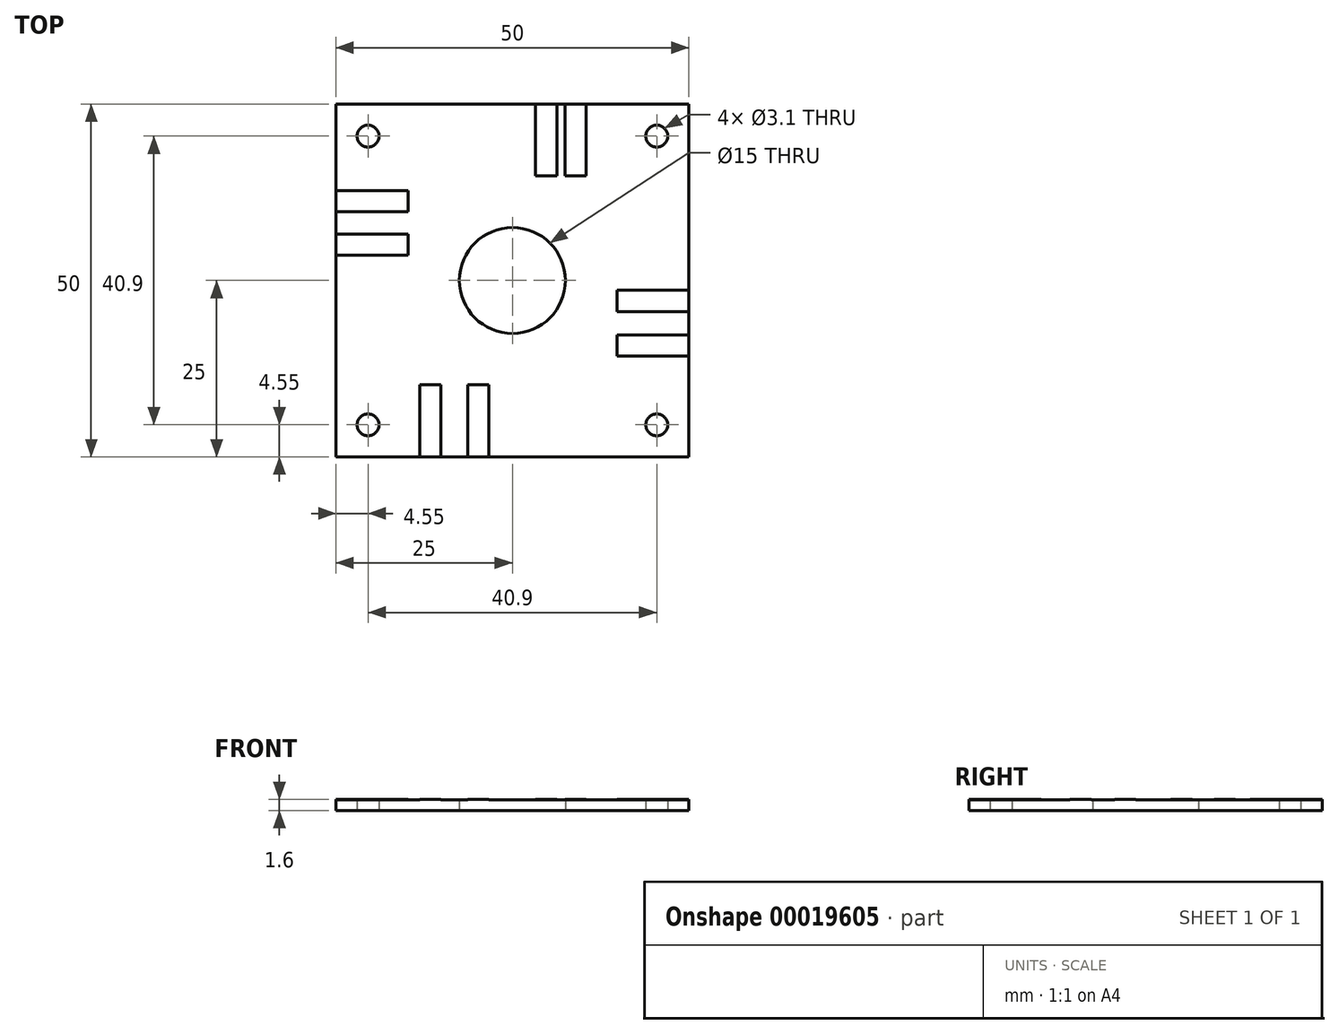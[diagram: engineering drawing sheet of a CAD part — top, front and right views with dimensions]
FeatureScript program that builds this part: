
annotation { "Feature Type Name" : "Feature", "Feature Type Description" : "" }
export const myFeature = defineFeature(function(context is Context, id is Id, definition is map)
    precondition{}
    {
        {
            var Q0;
            Q0=qCreatedBy(makeId("Top.planeOp"),FACE);
            var sketch = newSketch(context, id + "F0", { "sketchPlane" : qUnion([Q0])});
            skLineSegment(sketch, "E0.rect.bottom", {"start": v(-25, 25) * mm, "end": v(25, 25) * mm});
            skLineSegment(sketch, "E0.rect.top", {"start": v(-25, -25) * mm, "end": v(25, -25) * mm});
            skLineSegment(sketch, "E0.rect.left", {"start": v(-25, 25) * mm, "end": v(-25, -25) * mm});
            skLineSegment(sketch, "E0.rect.right", {"start": v(25, 25) * mm, "end": v(25, -25) * mm});
            skPoint(sketch, "E0.rect.middle", {"position": v(0, 0) * mm});
            skCircle(sketch, "E1", {"center": v(0, 0) * mm, "radius": 7.5 * mm});
            skCircle(sketch, "E2", {"center": v(-20.45, 20.45) * mm, "radius": 1.55 * mm});
            skCircle(sketch, "E3", {"center": v(-20.45, -20.45) * mm, "radius": 1.55 * mm});
            skCircle(sketch, "E4", {"center": v(20.45, -20.45) * mm, "radius": 1.55 * mm});
            skCircle(sketch, "E5", {"center": v(20.45, 20.45) * mm, "radius": 1.55 * mm});
            skSolve(sketch);
        }
        {
            var Q0;
            Q0=makeQuery(id+"F0.imprint","IMPRINT",FACE,{"disambiguationData":[TD([[makeQuery(id+"F0.imprint","IMPRINT",EDGE,{"derivedFrom":sQuery(id+"F0.wireOp",EDGE,"E0.rect.bottom")}),-1.0]])]});
            extrude(context, id + "F1", {"entities" : qUnion([Q0]), "depth" : 1.5 * mm});
        }
        {
            var Q0;
            Q0=makeQuery(id+"F1.opExtrude","CAP_FACE",FACE,{"disambiguationData":[OSD([sQuery(id+"F0.wireOp",EDGE,"E0.rect.bottom"),sQuery(id+"F0.wireOp",EDGE,"E0.rect.top"),sQuery(id+"F0.wireOp",EDGE,"E0.rect.left"),sQuery(id+"F0.wireOp",EDGE,"E0.rect.right"),sQuery(id+"F0.wireOp",EDGE,"E1"),sQuery(id+"F0.wireOp",EDGE,"E2"),sQuery(id+"F0.wireOp",EDGE,"E3"),sQuery(id+"F0.wireOp",EDGE,"E4"),sQuery(id+"F0.wireOp",EDGE,"E5")])],"isStart":false});
            var sketch = newSketch(context, id + "F2", { "sketchPlane" : qUnion([Q0])});
            skLineSegment(sketch, "E6.bottom", {"start": v(-13.15, -25) * mm, "end": v(-10.15, -25) * mm});
            skLineSegment(sketch, "E6.top", {"start": v(-13.15, -14.8) * mm, "end": v(-10.15, -14.8) * mm});
            skLineSegment(sketch, "E6.left", {"start": v(-13.15, -25) * mm, "end": v(-13.15, -14.8) * mm});
            skLineSegment(sketch, "E6.right", {"start": v(-10.15, -25) * mm, "end": v(-10.15, -14.8) * mm});
            skLineSegment(sketch, "E7.bottom", {"start": v(-6.35, -25) * mm, "end": v(-3.35, -25) * mm});
            skLineSegment(sketch, "E7.top", {"start": v(-6.35, -14.8) * mm, "end": v(-3.35, -14.8) * mm});
            skLineSegment(sketch, "E7.left", {"start": v(-6.35, -25) * mm, "end": v(-6.35, -14.8) * mm});
            skLineSegment(sketch, "E7.right", {"start": v(-3.35, -25) * mm, "end": v(-3.35, -14.8) * mm});
            skLineSegment(sketch, "E8.bottom", {"start": v(-25, 12.73) * mm, "end": v(-14.8, 12.73) * mm});
            skLineSegment(sketch, "E8.top", {"start": v(-25, 9.73) * mm, "end": v(-14.8, 9.73) * mm});
            skLineSegment(sketch, "E8.left", {"start": v(-25, 12.73) * mm, "end": v(-25, 9.73) * mm});
            skLineSegment(sketch, "E8.right", {"start": v(-14.8, 12.73) * mm, "end": v(-14.8, 9.73) * mm});
            skLineSegment(sketch, "E9.bottom", {"start": v(-25, 6.59) * mm, "end": v(-14.8, 6.59) * mm});
            skLineSegment(sketch, "E9.top", {"start": v(-25, 3.59) * mm, "end": v(-14.8, 3.59) * mm});
            skLineSegment(sketch, "E9.left", {"start": v(-25, 6.59) * mm, "end": v(-25, 3.59) * mm});
            skLineSegment(sketch, "E9.right", {"start": v(-14.8, 6.59) * mm, "end": v(-14.8, 3.59) * mm});
            skLineSegment(sketch, "E10.bottom", {"start": v(10.43, 25) * mm, "end": v(7.43, 25) * mm});
            skLineSegment(sketch, "E10.top", {"start": v(10.43, 14.8) * mm, "end": v(7.43, 14.8) * mm});
            skLineSegment(sketch, "E10.left", {"start": v(10.43, 25) * mm, "end": v(10.43, 14.8) * mm});
            skLineSegment(sketch, "E10.right", {"start": v(7.43, 25) * mm, "end": v(7.43, 14.8) * mm});
            skLineSegment(sketch, "E11.bottom", {"start": v(6.28, 25) * mm, "end": v(3.28, 25) * mm});
            skLineSegment(sketch, "E11.top", {"start": v(6.28, 14.8) * mm, "end": v(3.28, 14.8) * mm});
            skLineSegment(sketch, "E11.left", {"start": v(6.28, 25) * mm, "end": v(6.28, 14.8) * mm});
            skLineSegment(sketch, "E11.right", {"start": v(3.28, 25) * mm, "end": v(3.28, 14.8) * mm});
            skLineSegment(sketch, "E12.bottom", {"start": v(25, -10.7) * mm, "end": v(14.8, -10.7) * mm});
            skLineSegment(sketch, "E12.top", {"start": v(25, -7.7) * mm, "end": v(14.8, -7.7) * mm});
            skLineSegment(sketch, "E12.left", {"start": v(25, -10.7) * mm, "end": v(25, -7.7) * mm});
            skLineSegment(sketch, "E12.right", {"start": v(14.8, -10.7) * mm, "end": v(14.8, -7.7) * mm});
            skLineSegment(sketch, "E13.bottom", {"start": v(25, -4.4) * mm, "end": v(14.8, -4.4) * mm});
            skLineSegment(sketch, "E13.top", {"start": v(25, -1.4) * mm, "end": v(14.8, -1.4) * mm});
            skLineSegment(sketch, "E13.left", {"start": v(25, -4.4) * mm, "end": v(25, -1.4) * mm});
            skLineSegment(sketch, "E13.right", {"start": v(14.8, -4.4) * mm, "end": v(14.8, -1.4) * mm});
            skSolve(sketch);
        }
        {
            var Q0;
            Q0 = qSketchRegion(id + "F2", true);
            extrude(context, id + "F3", {"entities" : qUnion([Q0]), "operationType" : NewBodyOperationType.ADD, "depth" : .1 * mm});
        }
        {
            var Q0;
            Q0 = qSketchRegion(id + "F2", true);
            extrude(context, id + "F4", {"entities" : qUnion([Q0]), "operationType" : NewBodyOperationType.ADD, "depth" : .1 * mm});
        }
    });
